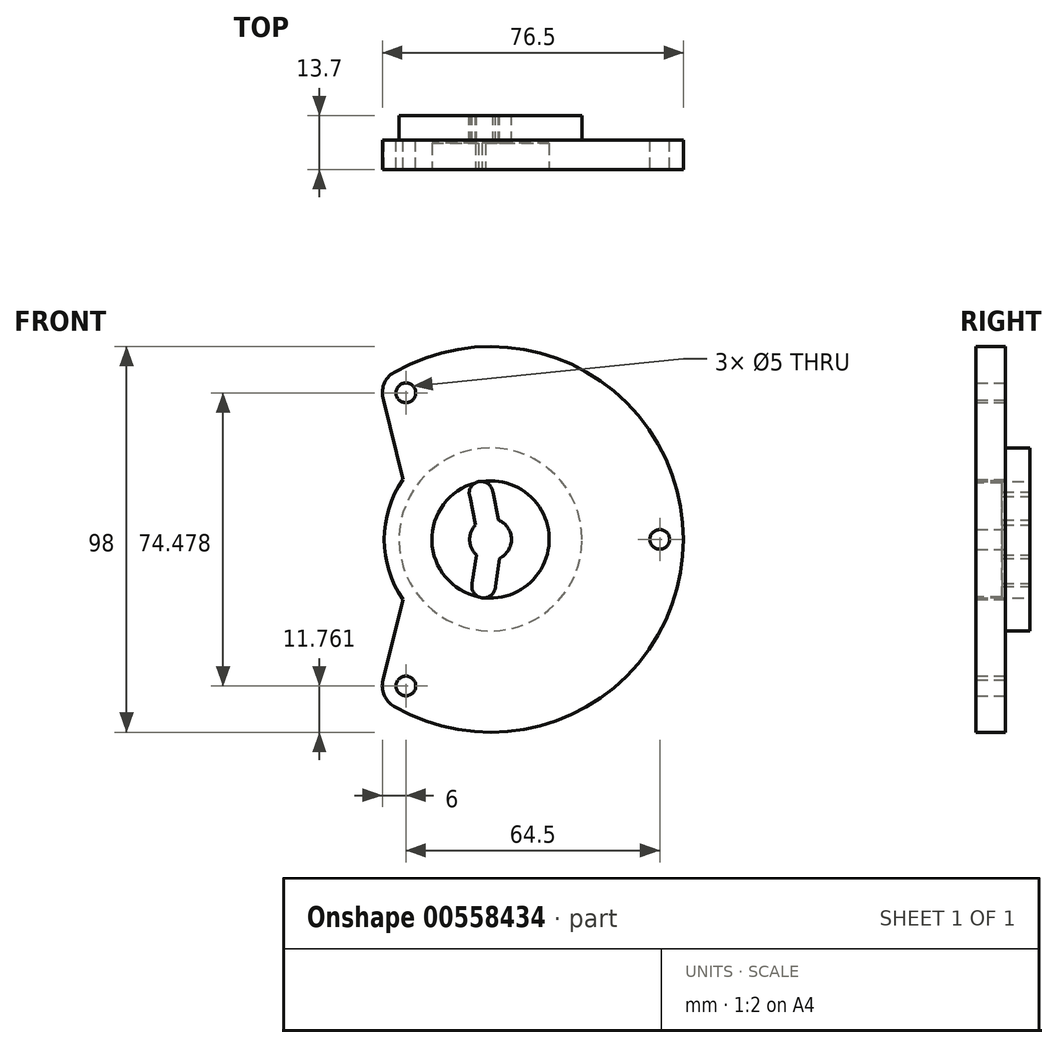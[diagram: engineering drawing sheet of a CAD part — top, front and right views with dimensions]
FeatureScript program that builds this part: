
annotation { "Feature Type Name" : "Feature", "Feature Type Description" : "" }
export const myFeature = defineFeature(function(context is Context, id is Id, definition is map)
    precondition{}
    {
        {
            var Q0;
            Q0=qCreatedBy(makeId("Front.planeOp"),FACE);
            var sketch = newSketch(context, id + "F0", { "sketchPlane" : qUnion([Q0])});
            skCircle(sketch, "E0", {"center": v(0, 0) * mm, "radius": 49 * mm});
            skArc(sketch, "E1", {"start": v(4.4, 2.98) * mm, "mid": v(3.36, 4.11) * mm, "end": v(2.04, 4.9) * mm});
            skCircle(sketch, "E2", {"center": v(43, 0) * mm, "radius": 2.5 * mm});
            skCircle(sketch, "E3.MirrorC", {"center": v(-21.5, -37.24) * mm, "radius": 2.5 * mm});
            skCircle(sketch, "E4", {"center": v(-21.5, 37.24) * mm, "radius": 2.5 * mm});
            skLineSegment(sketch, "E5.MirrorCS", {"start": v(-3.1, -4.3) * mm, "end": v(-3.68, -4.52) * mm});
            skArc(sketch, "E6.trimOffspring", {"start": v(2.31, -4.78) * mm, "mid": v(3.47, -4.02) * mm, "end": v(4.4, -2.98) * mm});
            skLineSegment(sketch, "E7.MirrorCS", {"start": v(2.31, -4.78) * mm, "end": v(1.24, -12.01) * mm});
            skArc(sketch, "E8.MirrorCS", {"start": v(-3.6, -3.9) * mm, "mid": v(-5.3, -0.15) * mm, "end": v(-3.8, 3.7) * mm});
            skLineSegment(sketch, "E9.MirrorCS", {"start": v(-3.8, 3.7) * mm, "end": v(-5.27, 10.86) * mm});
            skArc(sketch, "E10.MirrorCS", {"start": v(-5.27, 10.86) * mm, "mid": v(-3.02, 14.7) * mm, "end": v(0.57, 12.06) * mm});
            skLineSegment(sketch, "E11.MirrorCS", {"start": v(-3.6, -3.9) * mm, "end": v(-4.66, -11.13) * mm});
            skLineSegment(sketch, "E12.MirrorCS", {"start": v(2.04, 4.9) * mm, "end": v(0.57, 12.06) * mm});
            skArc(sketch, "E13.MirrorCS", {"start": v(-4.66, -11.13) * mm, "mid": v(-2.2, -14.84) * mm, "end": v(1.24, -12.01) * mm});
            skArc(sketch, "E14.MirrorCS", {"start": v(2.04, 4.9) * mm, "mid": v(5.3, 0.15) * mm, "end": v(2.31, -4.78) * mm});
            skArc(sketch, "E15.trimOffspring", {"start": v(-3.8, 3.7) * mm, "mid": v(-4.64, 2.6) * mm, "end": v(-5.15, 1.3) * mm});
            skSolve(sketch);
        }
        {
            var Q0;
            Q0=makeQuery(id+"F0.imprint","IMPRINT",FACE,{"disambiguationData":[TD([[makeQuery(id+"F0.imprint","IMPRINT",EDGE,{"derivedFrom":sQuery(id+"F0.wireOp",EDGE,"E0")}),1.0]])]});
            extrude(context, id + "F1", {"entities" : qUnion([Q0]), "depth" : 6.7 * mm, "offsetDistance" : 25 * mm, "hasSecondDirection" : true, "secondDirectionOppositeDirection" : true, "secondDirectionDepth" : 7 * mm});
        }
        {
            var Q0;
            Q0=makeQuery(id+"F1.opExtrude","CAP_FACE",FACE,{"disambiguationData":[OSD([sQuery(id+"F0.wireOp",EDGE,"E0"),sQuery(id+"F0.wireOp",EDGE,"E1"),sQuery(id+"F0.wireOp",EDGE,"E2"),sQuery(id+"F0.wireOp",EDGE,"E3.MirrorC"),sQuery(id+"F0.wireOp",EDGE,"E4"),sQuery(id+"F0.wireOp",EDGE,"E6.trimOffspring"),sQuery(id+"F0.wireOp",EDGE,"E7.MirrorCS"),sQuery(id+"F0.wireOp",EDGE,"E8.MirrorCS"),sQuery(id+"F0.wireOp",EDGE,"E9.MirrorCS"),sQuery(id+"F0.wireOp",EDGE,"E10.MirrorCS"),sQuery(id+"F0.wireOp",EDGE,"E11.MirrorCS"),sQuery(id+"F0.wireOp",EDGE,"E12.MirrorCS"),sQuery(id+"F0.wireOp",EDGE,"E13.MirrorCS"),sQuery(id+"F0.wireOp",EDGE,"E14.MirrorCS")])],"isStart":true});
            var sketch = newSketch(context, id + "F2", { "sketchPlane" : qUnion([Q0])});
            skCircle(sketch, "E16", {"center": v(0, 0) * mm, "radius": 55.35 * mm});
            skCircle(sketch, "E17", {"center": v(0, 0) * mm, "radius": 57.85 * mm});
            skSolve(sketch);
        }
        {
            var Q0;
            Q0=makeQuery(id+"F2.imprint","IMPRINT",FACE,{"disambiguationData":[TD([[makeQuery(id+"F2.imprint","IMPRINT",EDGE,{"derivedFrom":sQuery(id+"F2.wireOp",EDGE,"E16")}),-1.0]])]});
            extrude(context, id + "F3", {"entities" : qUnion([Q0]), "operationType" : NewBodyOperationType.REMOVE, "oppositeDirection" : true, "depth" : 3 * mm, "offsetDistance" : 25 * mm});
        }
        {
            var Q0;
            Q0=makeQuery(id+"F1.opExtrude","CAP_FACE",FACE,{"disambiguationData":[OSD([sQuery(id+"F0.wireOp",EDGE,"E0"),sQuery(id+"F0.wireOp",EDGE,"E1"),sQuery(id+"F0.wireOp",EDGE,"E2"),sQuery(id+"F0.wireOp",EDGE,"E3.MirrorC"),sQuery(id+"F0.wireOp",EDGE,"E4"),sQuery(id+"F0.wireOp",EDGE,"E6.trimOffspring"),sQuery(id+"F0.wireOp",EDGE,"E7.MirrorCS"),sQuery(id+"F0.wireOp",EDGE,"E8.MirrorCS"),sQuery(id+"F0.wireOp",EDGE,"E9.MirrorCS"),sQuery(id+"F0.wireOp",EDGE,"E10.MirrorCS"),sQuery(id+"F0.wireOp",EDGE,"E11.MirrorCS"),sQuery(id+"F0.wireOp",EDGE,"E12.MirrorCS"),sQuery(id+"F0.wireOp",EDGE,"E13.MirrorCS"),sQuery(id+"F0.wireOp",EDGE,"E14.MirrorCS")])],"isStart":false});
            var sketch = newSketch(context, id + "F4", { "sketchPlane" : qUnion([Q0])});
            skCircle(sketch, "E18", {"center": v(0, 0) * mm, "radius": 14.9 * mm});
            skLineSegment(sketch, "E19", {"start": v(0, 0) * mm, "end": v(30.07, 0) * mm});
            skSolve(sketch);
        }
        {
            var Q0;
            Q0 = qSketchRegion(id + "F4", true);
            extrude(context, id + "F5", {"entities" : qUnion([Q0]), "operationType" : NewBodyOperationType.REMOVE, "oppositeDirection" : true, "depth" : 6.65 * mm, "offsetDistance" : 25 * mm});
        }
        {
            var Q0;
            Q0=makeQuery(id+"F1.opExtrude","CAP_FACE",FACE,{"disambiguationData":[OSD([sQuery(id+"F0.wireOp",EDGE,"E0"),sQuery(id+"F0.wireOp",EDGE,"E1"),sQuery(id+"F0.wireOp",EDGE,"E2"),sQuery(id+"F0.wireOp",EDGE,"E3.MirrorC"),sQuery(id+"F0.wireOp",EDGE,"E4"),sQuery(id+"F0.wireOp",EDGE,"E6.trimOffspring"),sQuery(id+"F0.wireOp",EDGE,"E7.MirrorCS"),sQuery(id+"F0.wireOp",EDGE,"E8.MirrorCS"),sQuery(id+"F0.wireOp",EDGE,"E9.MirrorCS"),sQuery(id+"F0.wireOp",EDGE,"E10.MirrorCS"),sQuery(id+"F0.wireOp",EDGE,"E11.MirrorCS"),sQuery(id+"F0.wireOp",EDGE,"E12.MirrorCS"),sQuery(id+"F0.wireOp",EDGE,"E13.MirrorCS"),sQuery(id+"F0.wireOp",EDGE,"E14.MirrorCS")])],"isStart":true});
            var sketch = newSketch(context, id + "F6", { "sketchPlane" : qUnion([Q0])});
            skArc(sketch, "E20", {"start": v(-46, 5.2) * mm, "mid": v(-49, -0.1) * mm, "end": v(-45.82, -5.3) * mm});
            skArc(sketch, "E21", {"start": v(27.5, 37.03) * mm, "mid": v(24.59, 42.38) * mm, "end": v(18.5, 42.44) * mm});
            skArc(sketch, "E22", {"start": v(18.5, -42.44) * mm, "mid": v(24.59, -42.38) * mm, "end": v(27.5, -37.03) * mm});
            skArc(sketch, "E23", {"start": v(-44.64, 5.77) * mm, "mid": v(-49, -0.18) * mm, "end": v(-44.3, -5.86) * mm});
            skLineSegment(sketch, "E24", {"start": v(-44.64, 5.77) * mm, "end": v(-24.33, 11.67) * mm});
            skArc(sketch, "E25", {"start": v(27.24, 35.48) * mm, "mid": v(24.5, 42.44) * mm, "end": v(17.1, 41.31) * mm});
            skLineSegment(sketch, "E26", {"start": v(17.1, 41.31) * mm, "end": v(2.06, 26.88) * mm});
            skArc(sketch, "E27", {"start": v(17.35, -41.57) * mm, "mid": v(24.55, -42.4) * mm, "end": v(27.3, -35.7) * mm});
            skLineSegment(sketch, "E28", {"start": v(27.4, 36.14) * mm, "end": v(22.27, 15.22) * mm});
            skLineSegment(sketch, "E29", {"start": v(27.3, -35.7) * mm, "end": v(22.28, -15.3) * mm});
            skLineSegment(sketch, "E30", {"start": v(-44.3, -5.86) * mm, "end": v(-24.38, -11.65) * mm});
            skLineSegment(sketch, "E31", {"start": v(17.35, -41.57) * mm, "end": v(2.11, -26.96) * mm});
            skArc(sketch, "E32", {"start": v(2.06, 26.88) * mm, "mid": v(-13.48, 23.35) * mm, "end": v(-24.33, 11.67) * mm});
            skArc(sketch, "E33.trimOffspring", {"start": v(-24.38, -11.65) * mm, "mid": v(-13.5, -23.42) * mm, "end": v(2.11, -26.96) * mm});
            skArc(sketch, "E34.trimOffspring", {"start": v(22.28, -15.3) * mm, "mid": v(27, -0.04) * mm, "end": v(22.27, 15.22) * mm});
            skSolve(sketch);
        }
        {
            var Q0;
            {var subQ3=sQuery(id+"F6.wireOp",EDGE,"E24");Q0=makeQuery(id+"F6.imprint","IMPRINT",FACE,{"disambiguationData":[TD([[makeQuery(id+"F6.imprint","IMPRINT",EDGE,{"derivedFrom":subQ3}),1.0]])]});}
            var Q1;
            {var subQ13=sQuery(id+"F6.wireOp",EDGE,"E29");Q1=makeQuery(id+"F6.imprint","IMPRINT",FACE,{"disambiguationData":[TD([[makeQuery(id+"F6.imprint","IMPRINT",EDGE,{"derivedFrom":subQ13}),-1.0]])]});}
            var Q2;
            {var subQ10=sQuery(id+"F6.wireOp",EDGE,"E30");Q2=makeQuery(id+"F6.imprint","IMPRINT",FACE,{"disambiguationData":[TD([[makeQuery(id+"F6.imprint","IMPRINT",EDGE,{"derivedFrom":subQ10}),-1.0]])]});}
            extrude(context, id + "F7", {"entities" : qUnion([Q0, Q1, Q2]), "operationType" : NewBodyOperationType.REMOVE, "oppositeDirection" : true, "depth" : 30.3 * mm, "offsetDistance" : 25 * mm});
        }
        {
            var Q0;
            Q0=makeQuery(id+"F1.opExtrude","CAP_FACE",FACE,{"disambiguationData":[OSD([sQuery(id+"F0.wireOp",EDGE,"E0"),sQuery(id+"F0.wireOp",EDGE,"E1"),sQuery(id+"F0.wireOp",EDGE,"E2"),sQuery(id+"F0.wireOp",EDGE,"E3.MirrorC"),sQuery(id+"F0.wireOp",EDGE,"E4"),sQuery(id+"F0.wireOp",EDGE,"E6.trimOffspring"),sQuery(id+"F0.wireOp",EDGE,"E7.MirrorCS"),sQuery(id+"F0.wireOp",EDGE,"E8.MirrorCS"),sQuery(id+"F0.wireOp",EDGE,"E9.MirrorCS"),sQuery(id+"F0.wireOp",EDGE,"E10.MirrorCS"),sQuery(id+"F0.wireOp",EDGE,"E11.MirrorCS"),sQuery(id+"F0.wireOp",EDGE,"E12.MirrorCS"),sQuery(id+"F0.wireOp",EDGE,"E13.MirrorCS"),sQuery(id+"F0.wireOp",EDGE,"E14.MirrorCS")])],"isStart":true});
            var sketch = newSketch(context, id + "F8", { "sketchPlane" : qUnion([Q0])});
            skCircle(sketch, "E35", {"center": v(0, 0) * mm, "radius": 23.25 * mm});
            skCircle(sketch, "E36", {"center": v(0, 0) * mm, "radius": 57.3 * mm});
            skSolve(sketch);
        }
        {
            var Q0;
            Q0=makeQuery(id+"F8.imprint","IMPRINT",FACE,{"disambiguationData":[TD([[makeQuery(id+"F8.imprint","IMPRINT",EDGE,{"derivedFrom":sQuery(id+"F8.wireOp",EDGE,"E36")}),1.0]])]});
            var Q1;
            Q1=makeQuery(id+"F8.imprint","IMPRINT",FACE,{"disambiguationData":[TD([[makeQuery(id+"F8.imprint","IMPRINT",EDGE,{"derivedFrom":sQuery(id+"F8.wireOp",EDGE,"E35")}),-1.0]])]});
            var Q2;
            Q2=sQuery(id+"F8.wireOp",EDGE,"E35");
            var Q3;
            Q3=sQuery(id+"F8.wireOp",EDGE,"E36");
            extrude(context, id + "F9", {"entities" : qUnion([Q0, Q1]), "operationType" : NewBodyOperationType.REMOVE, "surfaceEntities" : qUnion([Q2, Q3]), "oppositeDirection" : true, "depth" : 6.25 * mm, "offsetDistance" : 25 * mm});
        }
    });
